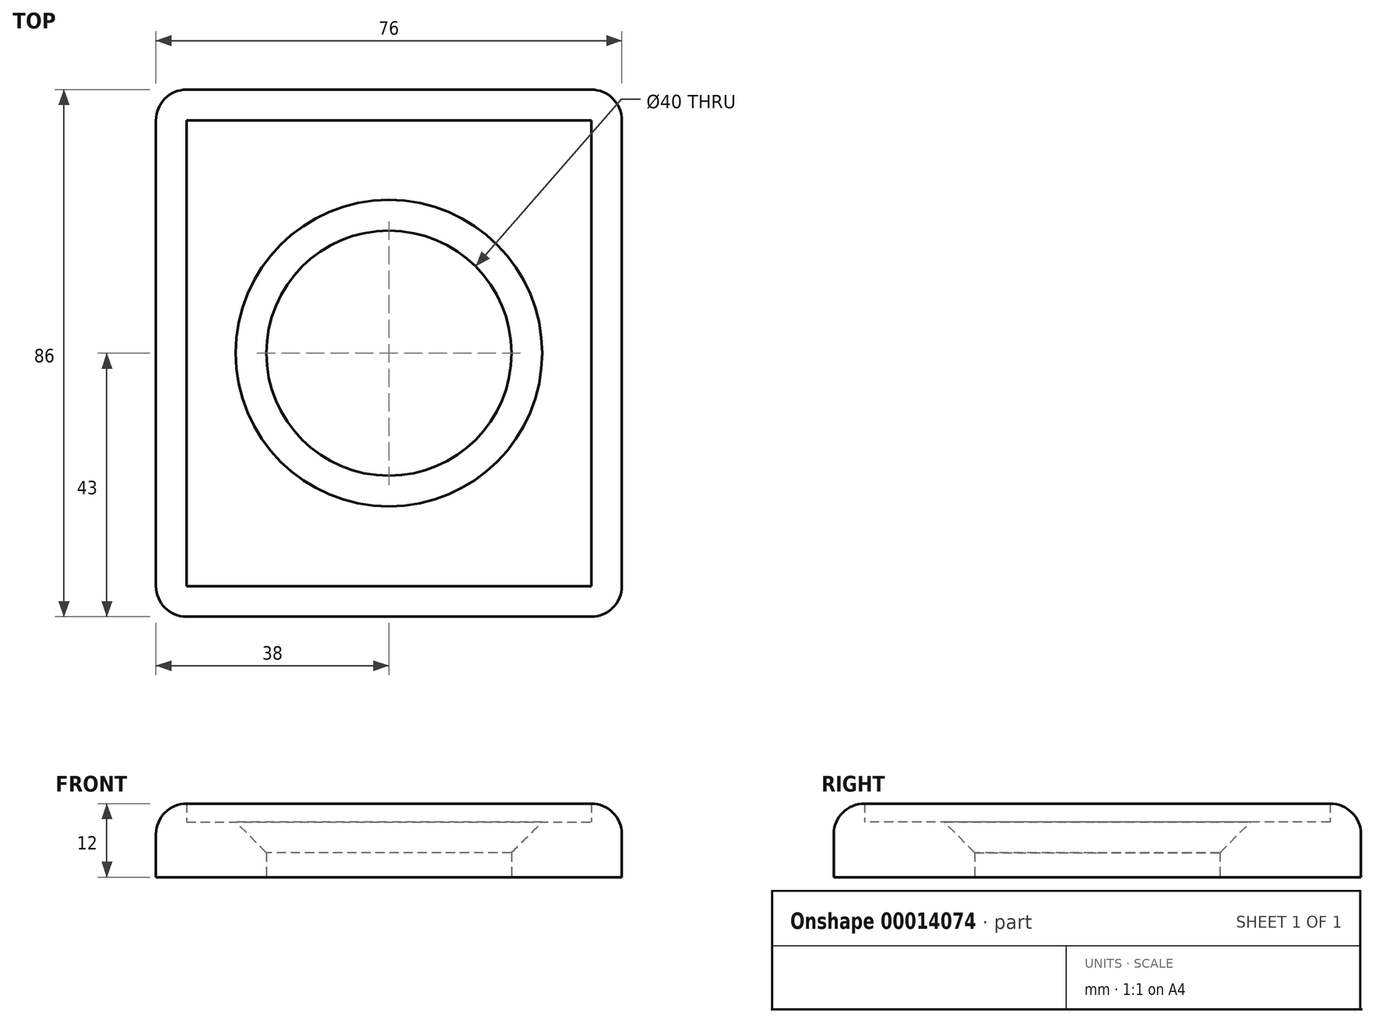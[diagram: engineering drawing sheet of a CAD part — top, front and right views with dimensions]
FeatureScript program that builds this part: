
annotation { "Feature Type Name" : "Feature", "Feature Type Description" : "" }
export const myFeature = defineFeature(function(context is Context, id is Id, definition is map)
    precondition{}
    {
        {
            var Q0;
            Q0=qCreatedBy(makeId("Top.planeOp"),FACE);
            var sketch = newSketch(context, id + "F0", { "sketchPlane" : qUnion([Q0])});
            skLineSegment(sketch, "E0.bottom", {"start": v(0, 0) * mm, "end": v(66, 0) * mm});
            skLineSegment(sketch, "E0.top", {"start": v(0, -76) * mm, "end": v(66, -76) * mm});
            skLineSegment(sketch, "E0.left", {"start": v(0, 0) * mm, "end": v(0, -76) * mm});
            skLineSegment(sketch, "E0.right", {"start": v(66, 0) * mm, "end": v(66, -76) * mm});
            skLineSegment(sketch, "E1", {"start": v(0, 0) * mm, "end": v(66, -76) * mm});
            skCircle(sketch, "E2", {"center": v(33, -38) * mm, "radius": 20 * mm});
            skLineSegment(sketch, "E3.rect.bottom", {"start": v(71, -81) * mm, "end": v(-5, -81) * mm});
            skLineSegment(sketch, "E3.rect.top", {"start": v(71, 5) * mm, "end": v(-5, 5) * mm});
            skLineSegment(sketch, "E3.rect.left", {"start": v(71, -81) * mm, "end": v(71, 5) * mm});
            skLineSegment(sketch, "E3.rect.right", {"start": v(-5, -81) * mm, "end": v(-5, 5) * mm});
            skSolve(sketch);
        }
        {
            var Q0;
            {var subQ5=sQuery(id+"F0.wireOp",EDGE,"E0.bottom");Q0=makeQuery(id+"F0.imprint","IMPRINT",FACE,{"disambiguationData":[TD([[makeQuery(id+"F0.imprint","IMPRINT",EDGE,{"derivedFrom":subQ5}),-1.0]])]});}
            var Q1;
            {var subQ4=sQuery(id+"F0.wireOp",EDGE,"E0.top");Q1=makeQuery(id+"F0.imprint","IMPRINT",FACE,{"disambiguationData":[TD([[makeQuery(id+"F0.imprint","IMPRINT",EDGE,{"derivedFrom":subQ4}),1.0]])]});}
            extrude(context, id + "F1", {"entities" : qUnion([Q0, Q1]), "depth" : 9 * mm});
        }
        {
            var Q0;
            Q0=makeQuery(id+"F0.imprint","IMPRINT",FACE,{"disambiguationData":[TD([[makeQuery(id+"F0.imprint","IMPRINT",EDGE,{"derivedFrom":sQuery(id+"F0.wireOp",EDGE,"E0.bottom")}),1.0]])]});
            extrude(context, id + "F2", {"entities" : qUnion([Q0]), "operationType" : NewBodyOperationType.ADD, "depth" : 12 * mm});
        }
        {
            var Q0;
            Q0=makeQuery(id+"F2.opExtrude","SWEPT_EDGE",EDGE,{"disambiguationData":[OSD([sQuery(id+"F0.wireOp",EDGE,"E3.rect.bottom"),sQuery(id+"F0.wireOp",EDGE,"E3.rect.right")])]});
            fillet(context, id + "F3", {"entities" : qUnion([Q0]), "radius" : 5 * mm, "tangentPropagation" : true, "allowEdgeOverflow" : false});
        }
        {
            var Q0;
            Q0=makeQuery(id+"F2.opExtrude","SWEPT_EDGE",EDGE,{"disambiguationData":[OSD([sQuery(id+"F0.wireOp",EDGE,"E3.rect.top"),sQuery(id+"F0.wireOp",EDGE,"E3.rect.right")])]});
            fillet(context, id + "F4", {"entities" : qUnion([Q0]), "radius" : 5 * mm, "tangentPropagation" : true, "allowEdgeOverflow" : false});
        }
        {
            var Q0;
            Q0=makeQuery(id+"F2.opExtrude","SWEPT_EDGE",EDGE,{"disambiguationData":[OSD([sQuery(id+"F0.wireOp",EDGE,"E3.rect.top"),sQuery(id+"F0.wireOp",EDGE,"E3.rect.left")])]});
            fillet(context, id + "F5", {"entities" : qUnion([Q0]), "radius" : 5 * mm, "tangentPropagation" : true, "allowEdgeOverflow" : false});
        }
        {
            var Q0;
            Q0=makeQuery(id+"F2.opExtrude","SWEPT_EDGE",EDGE,{"disambiguationData":[OSD([sQuery(id+"F0.wireOp",EDGE,"E3.rect.bottom"),sQuery(id+"F0.wireOp",EDGE,"E3.rect.left")])]});
            fillet(context, id + "F6", {"entities" : qUnion([Q0]), "radius" : 5 * mm, "tangentPropagation" : true, "allowEdgeOverflow" : false});
        }
        {
            var Q0;
            Q0=makeQuery(id+"F2.opExtrude","CAP_EDGE",EDGE,{"disambiguationData":[OSD([sQuery(id+"F0.wireOp",EDGE,"E3.rect.bottom")])],"isStart":false});
            fillet(context, id + "F7", {"entities" : qUnion([Q0]), "radius" : 5 * mm, "tangentPropagation" : true, "allowEdgeOverflow" : false});
        }
        {
            var Q0;
            Q0=makeQuery(id+"F1.opExtrude","CAP_EDGE",EDGE,{"disambiguationData":[OSD([sQuery(id+"F0.wireOp",EDGE,"E2")])],"isStart":false});
            chamfer(context, id + "F8", {"entities" : qUnion([Q0]), "width" : 5 * mm});
        }
    });
